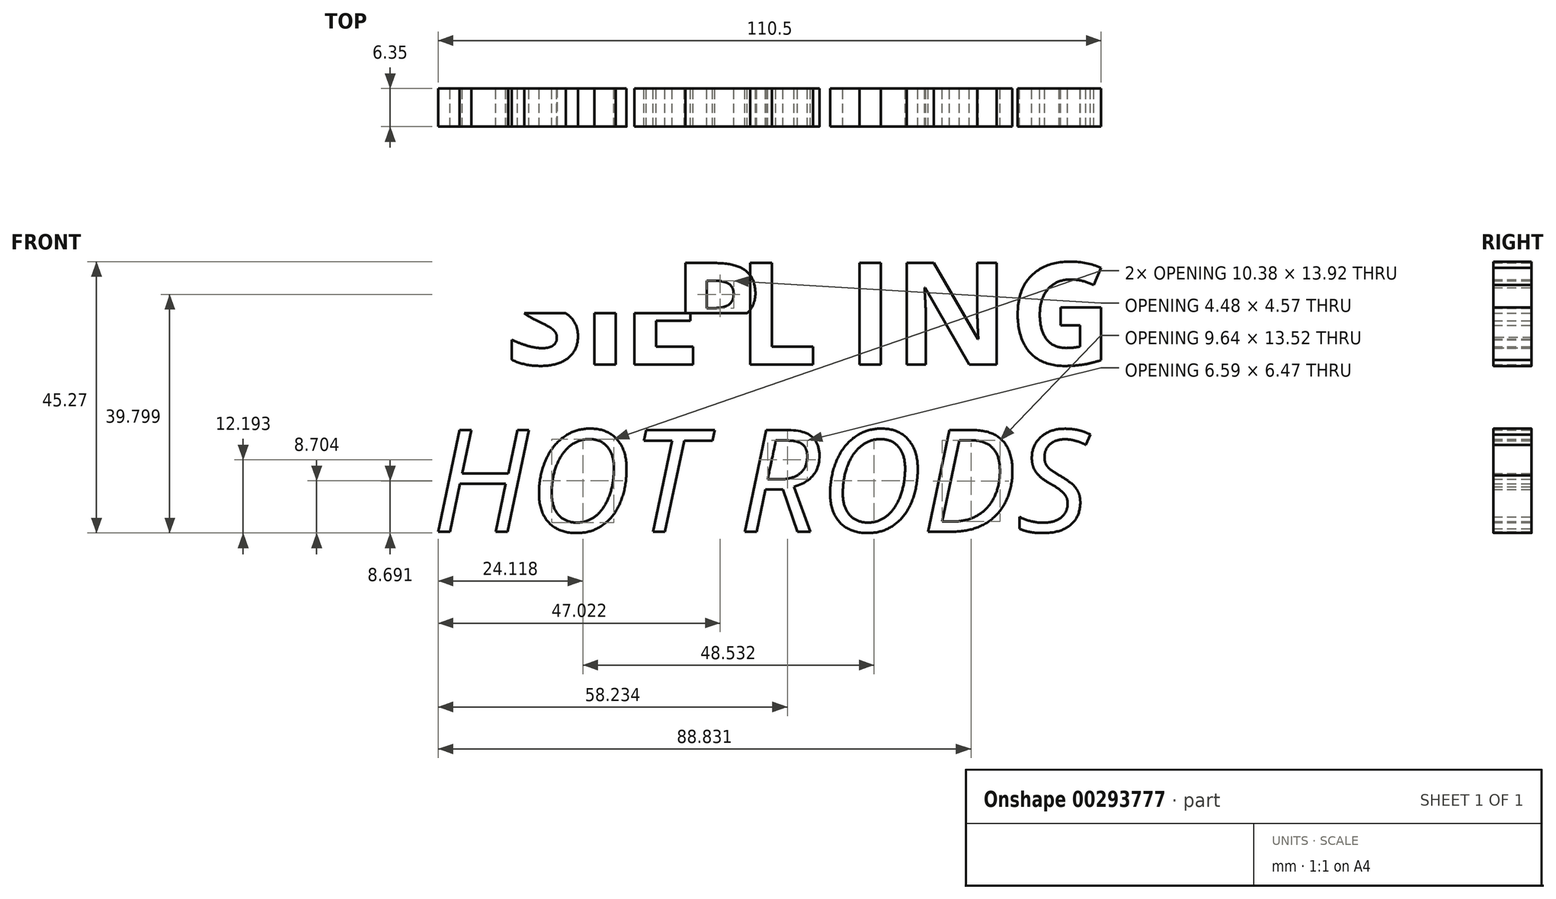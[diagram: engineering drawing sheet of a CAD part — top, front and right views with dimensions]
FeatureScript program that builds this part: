
annotation { "Feature Type Name" : "Feature", "Feature Type Description" : "" }
export const myFeature = defineFeature(function(context is Context, id is Id, definition is map)
    precondition{}
    {
        {
            var Q0;
            Q0=qCreatedBy(makeId("Front.planeOp"),FACE);
            var sketch = newSketch(context, id + "F0", { "sketchPlane" : qUnion([Q0])});
            skLineSegment(sketch, "E0.bottom", {"start": v(-60.33, 26.99) * mm, "end": v(60.33, 26.99) * mm});
            skLineSegment(sketch, "E0.top", {"start": v(-60.32, -26.99) * mm, "end": v(60.32, -26.99) * mm});
            skLineSegment(sketch, "E0.left", {"start": v(-60.32, 26.99) * mm, "end": v(-60.33, -26.99) * mm});
            skLineSegment(sketch, "E0.right", {"start": v(60.33, 26.99) * mm, "end": v(60.32, -26.99) * mm});
            skPoint(sketch, "E0.middle", {"position": v(0, 0) * mm});
            skLineSegment(sketch, "E1", {"start": v(-60.32, 0) * mm, "end": v(60.33, 0) * mm, "construction": true});
            skLineSegment(sketch, "E2", {"start": v(0, 26.99) * mm, "end": v(0, -26.99) * mm, "construction": true});
            skLineSegment(sketch, "E3", {"start": v(-67.02, 13.94) * mm, "end": v(66.4, 13.94) * mm, "construction": true});
            skLineSegment(sketch, "E4.MirrorCS", {"start": v(-67.02, -13.94) * mm, "end": v(66.4, -13.94) * mm, "construction": true});
            skLineSegment(sketch, "E5", {"start": v(-64.84, 13.94) * mm, "end": v(66.4, 13.94) * mm, "construction": true});
            skLineSegment(sketch, "E6.MirrorCS", {"start": v(-64.84, -13.94) * mm, "end": v(66.4, -13.94) * mm, "construction": true});
            skLineSegment(sketch, "E7", {"start": v(-55.38, 13.94) * mm, "end": v(0, 13.94) * mm, "construction": true});
            skLineSegment(sketch, "E8", {"start": v(0, 13.94) * mm, "end": v(-55.38, 13.94) * mm});
            skLineSegment(sketch, "E9", {"start": v(0, 13.94) * mm, "end": v(0, -29.46) * mm, "construction": true});
            skText(sketch, "E10", { "text": "STERLING", "fontName": "OpenSans-Bold.ttf"});
            skText(sketch, "E11", { "text": "HOT RODS", "fontName": "OpenSans-Italic.ttf"});
            const initialGuessF0  = {"E10": [-0.05652, 0.0054, 1, 0, 0.01707], "E11": [-0.05652, -0.02247, 1, 0, 0.01707]};
            skSetInitialGuess(sketch, initialGuessF0);
            skSolve(sketch);
        }
        {
            var Q0;
            Q0=makeQuery(id+"F0.imprint","IMPRINT",FACE,{"disambiguationData":[TD([[makeQuery(id+"F0.imprint","IMPRINT",EDGE,{"derivedFrom":sQuery(id+"F0.wireOp",EDGE,"E10.sketch_text.stroke-0")}),-1.0]])]});
            var Q1;
            Q1=makeQuery(id+"F0.imprint","IMPRINT",FACE,{"disambiguationData":[TD([[makeQuery(id+"F0.imprint","IMPRINT",EDGE,{"derivedFrom":sQuery(id+"F0.wireOp",EDGE,"E10.sketch_text.stroke-28")}),-1.0]])]});
            var Q2;
            Q2=makeQuery(id+"F0.imprint","IMPRINT",FACE,{"disambiguationData":[TD([[makeQuery(id+"F0.imprint","IMPRINT",EDGE,{"derivedFrom":sQuery(id+"F0.wireOp",EDGE,"E10.sketch_text.stroke-36")}),-1.0]])]});
            var Q3;
            Q3=makeQuery(id+"F0.imprint","IMPRINT",FACE,{"disambiguationData":[TD([[makeQuery(id+"F0.imprint","IMPRINT",EDGE,{"derivedFrom":sQuery(id+"F0.wireOp",EDGE,"E10.sketch_text.stroke-48")}),-1.0]])]});
            var Q4;
            Q4=makeQuery(id+"F0.imprint","IMPRINT",FACE,{"disambiguationData":[TD([[makeQuery(id+"F0.imprint","IMPRINT",EDGE,{"derivedFrom":sQuery(id+"F0.wireOp",EDGE,"E10.sketch_text.stroke-67")}),-1.0]])]});
            var Q5;
            Q5=makeQuery(id+"F0.imprint","IMPRINT",FACE,{"disambiguationData":[TD([[makeQuery(id+"F0.imprint","IMPRINT",EDGE,{"derivedFrom":sQuery(id+"F0.wireOp",EDGE,"E10.sketch_text.stroke-73")}),-1.0]])]});
            var Q6;
            Q6=makeQuery(id+"F0.imprint","IMPRINT",FACE,{"disambiguationData":[TD([[makeQuery(id+"F0.imprint","IMPRINT",EDGE,{"derivedFrom":sQuery(id+"F0.wireOp",EDGE,"E10.sketch_text.stroke-77")}),-1.0]])]});
            var Q7;
            Q7=makeQuery(id+"F0.imprint","IMPRINT",FACE,{"disambiguationData":[TD([[makeQuery(id+"F0.imprint","IMPRINT",EDGE,{"derivedFrom":sQuery(id+"F0.wireOp",EDGE,"E10.sketch_text.stroke-91")}),-1.0]])]});
            var Q8;
            Q8=makeQuery(id+"F0.imprint","IMPRINT",FACE,{"disambiguationData":[TD([[makeQuery(id+"F0.imprint","IMPRINT",EDGE,{"derivedFrom":sQuery(id+"F0.wireOp",EDGE,"E11.sketch_text.stroke-0")}),-1.0]])]});
            var Q9;
            Q9=makeQuery(id+"F0.imprint","IMPRINT",FACE,{"disambiguationData":[TD([[makeQuery(id+"F0.imprint","IMPRINT",EDGE,{"derivedFrom":sQuery(id+"F0.wireOp",EDGE,"E11.sketch_text.stroke-12")}),-1.0]])]});
            var Q10;
            Q10=makeQuery(id+"F0.imprint","IMPRINT",FACE,{"disambiguationData":[TD([[makeQuery(id+"F0.imprint","IMPRINT",EDGE,{"derivedFrom":sQuery(id+"F0.wireOp",EDGE,"E11.sketch_text.stroke-32")}),-1.0]])]});
            var Q11;
            Q11=makeQuery(id+"F0.imprint","IMPRINT",FACE,{"disambiguationData":[TD([[makeQuery(id+"F0.imprint","IMPRINT",EDGE,{"derivedFrom":sQuery(id+"F0.wireOp",EDGE,"E11.sketch_text.stroke-40")}),-1.0]])]});
            var Q12;
            Q12=makeQuery(id+"F0.imprint","IMPRINT",FACE,{"disambiguationData":[TD([[makeQuery(id+"F0.imprint","IMPRINT",EDGE,{"derivedFrom":sQuery(id+"F0.wireOp",EDGE,"E11.sketch_text.stroke-57")}),-1.0]])]});
            var Q13;
            Q13=makeQuery(id+"F0.imprint","IMPRINT",FACE,{"disambiguationData":[TD([[makeQuery(id+"F0.imprint","IMPRINT",EDGE,{"derivedFrom":sQuery(id+"F0.wireOp",EDGE,"E11.sketch_text.stroke-77")}),-1.0]])]});
            var Q14;
            Q14=makeQuery(id+"F0.imprint","IMPRINT",FACE,{"disambiguationData":[TD([[makeQuery(id+"F0.imprint","IMPRINT",EDGE,{"derivedFrom":sQuery(id+"F0.wireOp",EDGE,"E11.sketch_text.stroke-93")}),-1.0]])]});
            extrude(context, id + "F1", {"entities" : qUnion([Q0, Q1, Q2, Q3, Q4, Q5, Q6, Q7, Q8, Q9, Q10, Q11, Q12, Q13, Q14]), "depth" : 6.35 * mm});
        }
        {
            var Q0;
            Q0=makeQuery(id+"F1.opExtrude","SWEPT_BODY",BODY,{"disambiguationData":[OSD([sQuery(id+"F0.wireOp",EDGE,"E10.sketch_text.stroke-36"),sQuery(id+"F0.wireOp",EDGE,"E10.sketch_text.stroke-37"),sQuery(id+"F0.wireOp",EDGE,"E10.sketch_text.stroke-38"),sQuery(id+"F0.wireOp",EDGE,"E10.sketch_text.stroke-39"),sQuery(id+"F0.wireOp",EDGE,"E10.sketch_text.stroke-40"),sQuery(id+"F0.wireOp",EDGE,"E10.sketch_text.stroke-41"),sQuery(id+"F0.wireOp",EDGE,"E10.sketch_text.stroke-42"),sQuery(id+"F0.wireOp",EDGE,"E10.sketch_text.stroke-43"),sQuery(id+"F0.wireOp",EDGE,"E10.sketch_text.stroke-44"),sQuery(id+"F0.wireOp",EDGE,"E10.sketch_text.stroke-45"),sQuery(id+"F0.wireOp",EDGE,"E10.sketch_text.stroke-46"),sQuery(id+"F0.wireOp",EDGE,"E10.sketch_text.stroke-47")])]});
            var Q1;
            Q1=makeQuery(id+"F1.opExtrude","CAP_VERTEX",VERTEX,{"disambiguationData":[OSD([sQuery(id+"F0.wireOp",EDGE,"E10.sketch_text.stroke-56"),sQuery(id+"F0.wireOp",EDGE,"E10.sketch_text.stroke-57")])],"isStart":false});
            transform(context, id + "F2", {"entities" : qUnion([Q0]), "transformType" : TransformType.TRANSLATION_3D, "dx" : 4.83 * mm, "dy" : 0 * mm, "dz" : 0 * mm, "makeCopy" : false});
        }
        {
            var Q0;
            Q0=makeQuery(id+"F1.opExtrude","SWEPT_BODY",BODY,{"disambiguationData":[OSD([sQuery(id+"F0.wireOp",EDGE,"E10.sketch_text.stroke-28"),sQuery(id+"F0.wireOp",EDGE,"E10.sketch_text.stroke-29"),sQuery(id+"F0.wireOp",EDGE,"E10.sketch_text.stroke-30"),sQuery(id+"F0.wireOp",EDGE,"E10.sketch_text.stroke-31"),sQuery(id+"F0.wireOp",EDGE,"E10.sketch_text.stroke-32"),sQuery(id+"F0.wireOp",EDGE,"E10.sketch_text.stroke-33"),sQuery(id+"F0.wireOp",EDGE,"E10.sketch_text.stroke-34"),sQuery(id+"F0.wireOp",EDGE,"E10.sketch_text.stroke-35")])]});
            transform(context, id + "F3", {"entities" : qUnion([Q0]), "transformType" : TransformType.TRANSLATION_3D, "dx" : 8.9 * mm, "dy" : 0 * mm, "dz" : 0 * mm, "makeCopy" : false});
        }
        {
            var Q0;
            Q0=makeQuery(id+"F1.opExtrude","SWEPT_BODY",BODY,{"disambiguationData":[OSD([sQuery(id+"F0.wireOp",EDGE,"E10.sketch_text.stroke-0"),sQuery(id+"F0.wireOp",EDGE,"E10.sketch_text.stroke-1"),sQuery(id+"F0.wireOp",EDGE,"E10.sketch_text.stroke-2"),sQuery(id+"F0.wireOp",EDGE,"E10.sketch_text.stroke-3"),sQuery(id+"F0.wireOp",EDGE,"E10.sketch_text.stroke-4"),sQuery(id+"F0.wireOp",EDGE,"E10.sketch_text.stroke-5"),sQuery(id+"F0.wireOp",EDGE,"E10.sketch_text.stroke-6"),sQuery(id+"F0.wireOp",EDGE,"E10.sketch_text.stroke-7"),sQuery(id+"F0.wireOp",EDGE,"E10.sketch_text.stroke-8"),sQuery(id+"F0.wireOp",EDGE,"E10.sketch_text.stroke-9"),sQuery(id+"F0.wireOp",EDGE,"E10.sketch_text.stroke-10"),sQuery(id+"F0.wireOp",EDGE,"E10.sketch_text.stroke-11"),sQuery(id+"F0.wireOp",EDGE,"E10.sketch_text.stroke-12"),sQuery(id+"F0.wireOp",EDGE,"E10.sketch_text.stroke-13"),sQuery(id+"F0.wireOp",EDGE,"E10.sketch_text.stroke-14"),sQuery(id+"F0.wireOp",EDGE,"E10.sketch_text.stroke-15"),sQuery(id+"F0.wireOp",EDGE,"E10.sketch_text.stroke-16"),sQuery(id+"F0.wireOp",EDGE,"E10.sketch_text.stroke-17"),sQuery(id+"F0.wireOp",EDGE,"E10.sketch_text.stroke-18"),sQuery(id+"F0.wireOp",EDGE,"E10.sketch_text.stroke-19"),sQuery(id+"F0.wireOp",EDGE,"E10.sketch_text.stroke-20"),sQuery(id+"F0.wireOp",EDGE,"E10.sketch_text.stroke-21"),sQuery(id+"F0.wireOp",EDGE,"E10.sketch_text.stroke-22"),sQuery(id+"F0.wireOp",EDGE,"E10.sketch_text.stroke-23"),sQuery(id+"F0.wireOp",EDGE,"E10.sketch_text.stroke-24"),sQuery(id+"F0.wireOp",EDGE,"E10.sketch_text.stroke-25"),sQuery(id+"F0.wireOp",EDGE,"E10.sketch_text.stroke-26"),sQuery(id+"F0.wireOp",EDGE,"E10.sketch_text.stroke-27")])]});
            transform(context, id + "F4", {"entities" : qUnion([Q0]), "transformType" : TransformType.TRANSLATION_3D, "dx" : 12.2 * mm, "dy" : 0 * mm, "dz" : 0 * mm, "makeCopy" : false});
        }
        {
            var Q0;
            Q0=makeQuery(id+"F1.opExtrude","SWEPT_BODY",BODY,{"disambiguationData":[OSD([sQuery(id+"F0.wireOp",EDGE,"E10.sketch_text.stroke-67"),sQuery(id+"F0.wireOp",EDGE,"E10.sketch_text.stroke-68"),sQuery(id+"F0.wireOp",EDGE,"E10.sketch_text.stroke-69"),sQuery(id+"F0.wireOp",EDGE,"E10.sketch_text.stroke-70"),sQuery(id+"F0.wireOp",EDGE,"E10.sketch_text.stroke-71"),sQuery(id+"F0.wireOp",EDGE,"E10.sketch_text.stroke-72")])]});
            transform(context, id + "F5", {"entities" : qUnion([Q0]), "transformType" : TransformType.TRANSLATION_3D, "dx" : -4.83 * mm, "dy" : 0 * mm, "dz" : 0 * mm, "makeCopy" : false});
        }
    });
